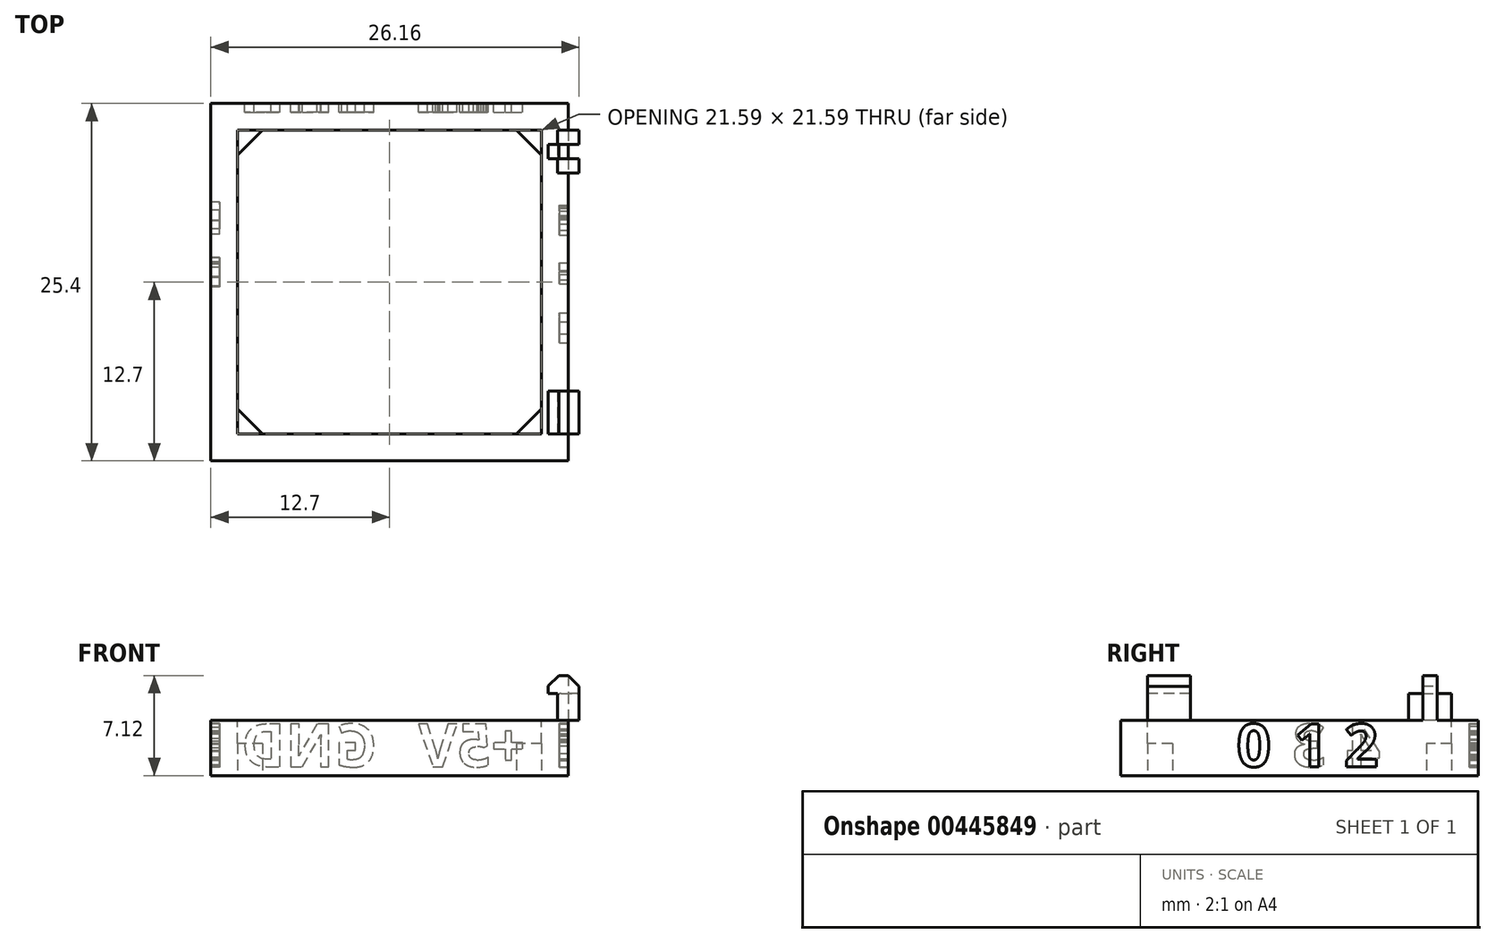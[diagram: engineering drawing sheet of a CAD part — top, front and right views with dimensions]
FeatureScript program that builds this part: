
annotation { "Feature Type Name" : "Feature", "Feature Type Description" : "" }
export const myFeature = defineFeature(function(context is Context, id is Id, definition is map)
    precondition{}
    {
        {
            var Q0;
            Q0=qCreatedBy(makeId("Top.planeOp"),FACE);
            var sketch = newSketch(context, id + "F0", { "sketchPlane" : qUnion([Q0])});
            skLineSegment(sketch, "E0.bottom", {"start": v(10.8, 10.8) * mm, "end": v(-10.8, 10.8) * mm});
            skLineSegment(sketch, "E0.top", {"start": v(10.8, -10.8) * mm, "end": v(-10.8, -10.8) * mm});
            skLineSegment(sketch, "E0.left", {"start": v(10.8, 10.8) * mm, "end": v(10.8, -10.8) * mm});
            skLineSegment(sketch, "E0.right", {"start": v(-10.8, 10.8) * mm, "end": v(-10.8, -10.8) * mm});
            skPoint(sketch, "E0.middle", {"position": v(0, 0) * mm});
            skLineSegment(sketch, "E1.0", {"start": v(12.7, -12.7) * mm, "end": v(-12.7, -12.7) * mm});
            skLineSegment(sketch, "E1.1", {"start": v(12.7, 12.7) * mm, "end": v(12.7, -12.7) * mm});
            skLineSegment(sketch, "E1.2", {"start": v(12.7, 12.7) * mm, "end": v(-12.7, 12.7) * mm});
            skLineSegment(sketch, "E1.3", {"start": v(-12.7, 12.7) * mm, "end": v(-12.7, -12.7) * mm});
            skSolve(sketch);
        }
        {
            var Q0;
            Q0=makeQuery(id+"F0.imprint","IMPRINT",FACE,{"disambiguationData":[TD([[makeQuery(id+"F0.imprint","IMPRINT",EDGE,{"derivedFrom":sQuery(id+"F0.wireOp",EDGE,"E0.bottom")}),1.0]])]});
            var sketch = newSketch(context, id + "F1", { "sketchPlane" : qUnion([Q0])});
            skPoint(sketch, "E2", {"position": v(0, 0) * mm});
            skSolve(sketch);
        }
        {
            var Q0;
            Q0=makeQuery(id+"F0.imprint","IMPRINT",FACE,{"disambiguationData":[TD([[makeQuery(id+"F0.imprint","IMPRINT",EDGE,{"derivedFrom":sQuery(id+"F0.wireOp",EDGE,"E0.bottom")}),-1.0]])]});
            extrude(context, id + "F2", {"entities" : qUnion([Q0]), "oppositeDirection" : true, "depth" : 2.3 * mm});
        }
        {
            var Q0;
            Q0=makeQuery(id+"F0.imprint","IMPRINT",FACE,{"disambiguationData":[TD([[makeQuery(id+"F0.imprint","IMPRINT",EDGE,{"derivedFrom":sQuery(id+"F0.wireOp",EDGE,"E0.bottom")}),-1.0]])]});
            extrude(context, id + "F3", {"entities" : qUnion([Q0]), "operationType" : NewBodyOperationType.ADD, "depth" : 1.65 * mm});
        }
        {
            var Q0;
            {var subQ0=sQuery(id+"F0.wireOp",EDGE,"E1.1");Q0=makeQuery(id+"F33ZesgtKe6OHiI_1.boolean.opBoolean","MERGE",FACE,{"derivedFrom":[makeQuery(id+"Fl4HXPqddT7Ymcp_1.boolean.opBoolean","MERGE",FACE,{"derivedFrom":[makeQuery(id+"F2.opExtrude","SWEPT_FACE",FACE,{"disambiguationData":[OSD([subQ0])]}),makeQuery(id+"Fl4HXPqddT7Ymcp_1.opExtrude","SWEPT_FACE",FACE,{"disambiguationData":[OSD([subQ0])]})]}),makeQuery(id+"F33ZesgtKe6OHiI_1.opExtrude","SWEPT_FACE",FACE,{"disambiguationData":[OSD([sQuery(id+"FHJWVWNGVrHaLrI_1.wireOp",EDGE,"lk0AvFoq-LB85-dOoa-LuWJ-0AeOwgkN9JTX.right")])]})]});}
            var sketch = newSketch(context, id + "F4", { "sketchPlane" : qUnion([Q0])});
            skText(sketch, "E3", { "text": "0", "fontName": "OpenSans-Bold.ttf"});
            skText(sketch, "E4", { "text": "1", "fontName": "OpenSans-Bold.ttf"});
            skText(sketch, "E5", { "text": "2", "fontName": "OpenSans-Bold.ttf"});
            skLineSegment(sketch, "E6.0.0", {"start": v(12.7, -2.29) * mm, "end": v(12.7, 1.65) * mm});
            skLineSegment(sketch, "E6.0.1", {"start": v(12.7, 1.65) * mm, "end": v(-12.7, 1.65) * mm});
            skLineSegment(sketch, "E6.0.2", {"start": v(-12.7, 1.65) * mm, "end": v(-12.7, -2.29) * mm});
            skLineSegment(sketch, "E6.0.3", {"start": v(-12.7, -2.29) * mm, "end": v(12.7, -2.29) * mm});
            skPoint(sketch, "E7.0", {"position": v(0, 0) * mm});
            const initialGuessF4  = {"E3": [-0.00445, -0.00165, 1, 0, 0.00305], "E4": [-0.00038, -0.00165, 1, 0, 0.00305], "E5": [0.00317, -0.00165, 1, 0, 0.00305]};
            skSetInitialGuess(sketch, initialGuessF4);
            skSolve(sketch);
        }
        {
            var Q0;
            Q0=makeQuery(id+"F4.imprint","IMPRINT",FACE,{"disambiguationData":[TD([[makeQuery(id+"F4.imprint","IMPRINT",EDGE,{"derivedFrom":sQuery(id+"F4.wireOp",EDGE,"E3.sketch_text.stroke-0")}),-1.0]])]});
            var Q1;
            Q1=makeQuery(id+"F4.imprint","IMPRINT",FACE,{"disambiguationData":[TD([[makeQuery(id+"F4.imprint","IMPRINT",EDGE,{"derivedFrom":sQuery(id+"F4.wireOp",EDGE,"E4.sketch_text.stroke-0")}),-1.0]])]});
            var Q2;
            Q2=makeQuery(id+"F4.imprint","IMPRINT",FACE,{"disambiguationData":[TD([[makeQuery(id+"F4.imprint","IMPRINT",EDGE,{"derivedFrom":sQuery(id+"F4.wireOp",EDGE,"E5.sketch_text.stroke-0")}),-1.0]])]});
            extrude(context, id + "F5", {"entities" : qUnion([Q0, Q1, Q2]), "operationType" : NewBodyOperationType.REMOVE, "oppositeDirection" : true, "depth" : 0.63 * mm});
        }
        {
            var Q0;
            {var subQ0=sQuery(id+"F0.wireOp",EDGE,"E1.3");Q0=makeQuery(id+"F33ZesgtKe6OHiI_1.boolean.opBoolean","MERGE",FACE,{"derivedFrom":[makeQuery(id+"Fl4HXPqddT7Ymcp_1.boolean.opBoolean","MERGE",FACE,{"derivedFrom":[makeQuery(id+"F2.opExtrude","SWEPT_FACE",FACE,{"disambiguationData":[OSD([subQ0])]}),makeQuery(id+"Fl4HXPqddT7Ymcp_1.opExtrude","SWEPT_FACE",FACE,{"disambiguationData":[OSD([subQ0])]})]}),makeQuery(id+"F33ZesgtKe6OHiI_1.opExtrude","SWEPT_FACE",FACE,{"disambiguationData":[OSD([sQuery(id+"FHJWVWNGVrHaLrI_1.wireOp",EDGE,"lk0AvFoq-LB85-dOoa-LuWJ-0AeOwgkN9JTX.left")])]})]});}
            var sketch = newSketch(context, id + "F6", { "sketchPlane" : qUnion([Q0])});
            skText(sketch, "E8", { "text": "4", "fontName": "OpenSans-Bold.ttf"});
            skText(sketch, "E9", { "text": "3", "fontName": "OpenSans-Bold.ttf"});
            skPoint(sketch, "E10.0", {"position": v(1.9, 1.4) * mm});
            skPoint(sketch, "E11.0", {"position": v(-1.9, 1.4) * mm});
            const initialGuessF6  = {"E8": [-0.00576, -0.00165, 1, 0, 0.00305], "E9": [-0.0019, -0.00165, 1, 0, 0.00305]};
            skSetInitialGuess(sketch, initialGuessF6);
            skSolve(sketch);
        }
        {
            var Q0;
            Q0=makeQuery(id+"F6.imprint","IMPRINT",FACE,{"disambiguationData":[TD([[makeQuery(id+"F6.imprint","IMPRINT",EDGE,{"derivedFrom":sQuery(id+"F6.wireOp",EDGE,"E8.sketch_text.stroke-0")}),-1.0]])]});
            var Q1;
            Q1=makeQuery(id+"F6.imprint","IMPRINT",FACE,{"disambiguationData":[TD([[makeQuery(id+"F6.imprint","IMPRINT",EDGE,{"derivedFrom":sQuery(id+"F6.wireOp",EDGE,"E9.sketch_text.stroke-0")}),-1.0]])]});
            extrude(context, id + "F7", {"entities" : qUnion([Q0, Q1]), "operationType" : NewBodyOperationType.REMOVE, "oppositeDirection" : true, "depth" : 0.63 * mm});
        }
        {
            var Q0;
            {var subQ0=sQuery(id+"F0.wireOp",EDGE,"E1.2");Q0=makeQuery(id+"F3.boolean.opBoolean","MERGE",FACE,{"derivedFrom":[makeQuery(id+"F2.opExtrude","SWEPT_FACE",FACE,{"disambiguationData":[OSD([subQ0])]}),makeQuery(id+"F3.opExtrude","SWEPT_FACE",FACE,{"disambiguationData":[OSD([subQ0])]})]});}
            var sketch = newSketch(context, id + "F8", { "sketchPlane" : qUnion([Q0])});
            skText(sketch, "E12", { "text": "+5V", "fontName": "OpenSans-Bold.ttf"});
            skText(sketch, "E13", { "text": "GND", "fontName": "OpenSans-Bold.ttf"});
            skLineSegment(sketch, "E14.0.0", {"start": v(-10.8, -2.29) * mm, "end": v(-10.8, 1.65) * mm});
            skLineSegment(sketch, "E14.0.2", {"start": v(-10.8, 1.65) * mm, "end": v(-10.8, -2.29) * mm});
            skLineSegment(sketch, "E15.0.0", {"start": v(10.8, -2.29) * mm, "end": v(10.8, 1.65) * mm});
            skLineSegment(sketch, "E15.0.2", {"start": v(10.8, 1.65) * mm, "end": v(10.8, -2.29) * mm});
            const initialGuessF8  = {"E12": [-0.00964, -0.00165, 1, 0, 0.00305], "E13": [0.00088, -0.00165, 1, 0, 0.00305]};
            skSetInitialGuess(sketch, initialGuessF8);
            skSolve(sketch);
        }
        {
            var Q0;
            Q0=qSketchRegion(id+"F8",true);
            extrude(context, id + "F9", {"entities" : qUnion([Q0]), "operationType" : NewBodyOperationType.REMOVE, "oppositeDirection" : true, "depth" : 0.63 * mm});
        }
        {
            var Q0;
            Q0=makeQuery(id+"F2.opExtrude","CAP_FACE",FACE,{"disambiguationData":[OSD([sQuery(id+"F0.wireOp",EDGE,"E0.bottom"),sQuery(id+"F0.wireOp",EDGE,"E0.top"),sQuery(id+"F0.wireOp",EDGE,"E0.left"),sQuery(id+"F0.wireOp",EDGE,"E0.right"),sQuery(id+"F0.wireOp",EDGE,"E1.0"),sQuery(id+"F0.wireOp",EDGE,"E1.1"),sQuery(id+"F0.wireOp",EDGE,"E1.2"),sQuery(id+"F0.wireOp",EDGE,"E1.3")])],"isStart":false});
            var sketch = newSketch(context, id + "F10", { "sketchPlane" : qUnion([Q0])});
            skLineSegment(sketch, "E16", {"start": v(-10.8, 9.02) * mm, "end": v(-9.02, 10.8) * mm});
            skLineSegment(sketch, "E17", {"start": v(-9.02, 10.8) * mm, "end": v(-10.8, 10.8) * mm});
            skLineSegment(sketch, "E18", {"start": v(-10.8, 10.8) * mm, "end": v(-10.8, 9.02) * mm});
            skLineSegment(sketch, "E19", {"start": v(0, 10.8) * mm, "end": v(0, 0) * mm});
            skLineSegment(sketch, "E20", {"start": v(0, 0) * mm, "end": v(10.8, 0) * mm});
            skLineSegment(sketch, "E21.MirrorCS", {"start": v(10.8, 10.8) * mm, "end": v(10.8, 9.02) * mm});
            skLineSegment(sketch, "E22.MirrorCS", {"start": v(9.02, 10.8) * mm, "end": v(10.8, 10.8) * mm});
            skLineSegment(sketch, "E23.MirrorCS", {"start": v(10.8, 9.02) * mm, "end": v(9.02, 10.8) * mm});
            skLineSegment(sketch, "E24.MirrorCS", {"start": v(10.8, -10.8) * mm, "end": v(10.8, -9.02) * mm});
            skLineSegment(sketch, "E25.MirrorCS", {"start": v(10.8, -9.02) * mm, "end": v(9.02, -10.8) * mm});
            skLineSegment(sketch, "E26.MirrorCS", {"start": v(-9.02, -10.8) * mm, "end": v(-10.8, -10.8) * mm});
            skLineSegment(sketch, "E27.MirrorCS", {"start": v(9.02, -10.8) * mm, "end": v(10.8, -10.8) * mm});
            skLineSegment(sketch, "E28.MirrorCS", {"start": v(-10.8, -9.02) * mm, "end": v(-9.02, -10.8) * mm});
            skLineSegment(sketch, "E29.MirrorCS", {"start": v(-10.8, -10.8) * mm, "end": v(-10.8, -9.02) * mm});
            skSolve(sketch);
        }
        {
            var Q0;
            Q0=makeQuery(id+"F10.imprint","IMPRINT",FACE,{"disambiguationData":[TD([[makeQuery(id+"F10.imprint","IMPRINT",EDGE,{"derivedFrom":sQuery(id+"F10.wireOp",EDGE,"E16")}),1.0]])]});
            var Q1;
            Q1=makeQuery(id+"F10.imprint","IMPRINT",FACE,{"disambiguationData":[TD([[makeQuery(id+"F10.imprint","IMPRINT",EDGE,{"derivedFrom":sQuery(id+"F10.wireOp",EDGE,"E26.MirrorCS")}),-1.0]])]});
            var Q2;
            Q2=makeQuery(id+"F10.imprint","IMPRINT",FACE,{"disambiguationData":[TD([[makeQuery(id+"F10.imprint","IMPRINT",EDGE,{"derivedFrom":sQuery(id+"F10.wireOp",EDGE,"E21.MirrorCS")}),1.0]])]});
            var Q3;
            Q3=makeQuery(id+"F10.imprint","IMPRINT",FACE,{"disambiguationData":[TD([[makeQuery(id+"F10.imprint","IMPRINT",EDGE,{"derivedFrom":sQuery(id+"F10.wireOp",EDGE,"E24.MirrorCS")}),1.0]])]});
            var Q4;
            Q4=sQuery(id+"F0.wireOp",VERTEX,"E0.right.end");
            extrude(context, id + "F11", {"entities" : qUnion([Q0, Q1, Q2, Q3]), "operationType" : NewBodyOperationType.ADD, "endBound" : BoundingType.UP_TO_VERTEX, "oppositeDirection" : true, "endBoundEntityVertex" : qUnion([Q4]), "depth" : 25.4 * mm});
        }
        {
            var Q0;
            {var subQ2=sQuery(id+"F0.wireOp",EDGE,"E1.1");var subQ3=sQuery(id+"F0.wireOp",EDGE,"E1.0");Q0=makeQuery(id+"F5.boolean.opBoolean","SPLIT",FACE,{"disambiguationData":[TD([makeQuery(id+"F2.opExtrude","SWEPT_FACE",FACE,{"disambiguationData":[OSD([subQ3])]})])],"derivedFrom":makeQuery(id+"F3.boolean.opBoolean","MERGE",FACE,{"derivedFrom":[makeQuery(id+"F2.opExtrude","SWEPT_FACE",FACE,{"disambiguationData":[OSD([subQ2])]}),makeQuery(id+"F3.opExtrude","SWEPT_FACE",FACE,{"disambiguationData":[OSD([subQ2])]})]})});}
            var sketch = newSketch(context, id + "F12", { "sketchPlane" : qUnion([Q0])});
            skLineSegment(sketch, "E30.bottom", {"start": v(7.75, -1.52) * mm, "end": v(10.8, -1.52) * mm});
            skLineSegment(sketch, "E30.top", {"start": v(7.75, 4.83) * mm, "end": v(10.8, 4.83) * mm});
            skLineSegment(sketch, "E30.left", {"start": v(7.75, -1.52) * mm, "end": v(7.75, 4.83) * mm});
            skLineSegment(sketch, "E30.right", {"start": v(10.8, -1.52) * mm, "end": v(10.8, 4.83) * mm});
            skLineSegment(sketch, "E31.bottom", {"start": v(7.75, 4.83) * mm, "end": v(8.76, 4.83) * mm});
            skLineSegment(sketch, "E31.top", {"start": v(7.75, -1.52) * mm, "end": v(8.76, -1.52) * mm});
            skLineSegment(sketch, "E31.left", {"start": v(7.75, 4.83) * mm, "end": v(7.75, -1.52) * mm});
            skLineSegment(sketch, "E31.right", {"start": v(8.76, 4.83) * mm, "end": v(8.76, -1.52) * mm});
            skLineSegment(sketch, "E32.bottom", {"start": v(10.8, 4.83) * mm, "end": v(9.78, 4.83) * mm});
            skLineSegment(sketch, "E32.top", {"start": v(10.8, -1.52) * mm, "end": v(9.78, -1.52) * mm});
            skLineSegment(sketch, "E32.left", {"start": v(10.8, 4.83) * mm, "end": v(10.8, -1.52) * mm});
            skLineSegment(sketch, "E32.right", {"start": v(9.78, 4.83) * mm, "end": v(9.78, -1.52) * mm});
            skLineSegment(sketch, "E33.top", {"start": v(7.75, 3.56) * mm, "end": v(10.8, 3.56) * mm});
            skLineSegment(sketch, "E33.left", {"start": v(7.75, 4.83) * mm, "end": v(7.75, 3.56) * mm});
            skLineSegment(sketch, "E33.right", {"start": v(10.8, 4.83) * mm, "end": v(10.8, 3.56) * mm});
            skLineSegment(sketch, "E34", {"start": v(0, 1.65) * mm, "end": v(0, -2.29) * mm});
            skLineSegment(sketch, "E35.MirrorCS", {"start": v(-7.75, 4.83) * mm, "end": v(-7.75, 3.56) * mm});
            skLineSegment(sketch, "E36.MirrorCS", {"start": v(-10.8, 4.83) * mm, "end": v(-10.8, 3.56) * mm});
            skLineSegment(sketch, "E37.MirrorCS", {"start": v(-10.8, 4.83) * mm, "end": v(-9.78, 4.83) * mm});
            skLineSegment(sketch, "E38.MirrorCS", {"start": v(-7.75, 4.83) * mm, "end": v(-10.8, 4.83) * mm});
            skLineSegment(sketch, "E39.MirrorCS", {"start": v(-7.75, -1.52) * mm, "end": v(-7.75, 4.83) * mm});
            skLineSegment(sketch, "E40.MirrorCS", {"start": v(-10.8, -1.52) * mm, "end": v(-10.8, 4.83) * mm});
            skLineSegment(sketch, "E41.MirrorCS", {"start": v(-7.75, 4.83) * mm, "end": v(-8.76, 4.83) * mm});
            skLineSegment(sketch, "E42.MirrorCS", {"start": v(-7.75, 3.56) * mm, "end": v(-10.8, 3.56) * mm});
            skLineSegment(sketch, "E43.MirrorCS", {"start": v(-7.75, -1.52) * mm, "end": v(-10.8, -1.52) * mm});
            skLineSegment(sketch, "E44.MirrorCS", {"start": v(-7.75, -1.52) * mm, "end": v(-8.76, -1.52) * mm});
            skLineSegment(sketch, "E45.MirrorCS", {"start": v(-7.75, 4.83) * mm, "end": v(-7.75, -1.52) * mm});
            skLineSegment(sketch, "E46.MirrorCS", {"start": v(-8.76, 4.83) * mm, "end": v(-8.76, -1.52) * mm});
            skLineSegment(sketch, "E47.MirrorCS", {"start": v(-10.8, -1.52) * mm, "end": v(-9.78, -1.52) * mm});
            skLineSegment(sketch, "E48.MirrorCS", {"start": v(-10.8, 4.83) * mm, "end": v(-10.8, -1.52) * mm});
            skLineSegment(sketch, "E49.MirrorCS", {"start": v(-9.78, 4.83) * mm, "end": v(-9.78, -1.52) * mm});
            skSolve(sketch);
        }
        {
            var Q0;
            {var subQ0=sQuery(id+"F12.wireOp",EDGE,"E33.top");var subQ1=sQuery(id+"F12.wireOp",EDGE,"E31.right");var subQ2=makeQuery(id+"F12.imprint","INTERSECT",VERTEX,{"derivedFrom":[subQ1,subQ0]});Q0=makeQuery(id+"F12.imprint","IMPRINT",FACE,{"disambiguationData":[TD([[makeQuery(id+"F12.imprint","IMPRINT",EDGE,{"disambiguationData":[TD([[subQ2,-1.0]])],"derivedFrom":subQ1}),1.0]])]});}
            var Q1;
            {var subQ0=sQuery(id+"F12.wireOp",EDGE,"E33.top");var subQ5=sQuery(id+"F12.wireOp",EDGE,"E32.right");var subQ6=makeQuery(id+"F12.imprint","INTERSECT",VERTEX,{"derivedFrom":[subQ5,subQ0]});Q1=makeQuery(id+"F12.imprint","IMPRINT",FACE,{"disambiguationData":[TD([[makeQuery(id+"F12.imprint","IMPRINT",EDGE,{"disambiguationData":[TD([[subQ6,-1.0]])],"derivedFrom":subQ5}),1.0]])]});}
            var Q2;
            {var subQ0=sQuery(id+"F12.wireOp",EDGE,"E33.top");var subQ5=sQuery(id+"F12.wireOp",EDGE,"E31.right");var subQ6=makeQuery(id+"F12.imprint","INTERSECT",VERTEX,{"derivedFrom":[subQ5,subQ0]});Q2=makeQuery(id+"F12.imprint","IMPRINT",FACE,{"disambiguationData":[TD([[makeQuery(id+"F12.imprint","IMPRINT",EDGE,{"disambiguationData":[TD([[subQ6,-1.0]])],"derivedFrom":subQ5}),-1.0]])]});}
            var Q3;
            {var subQ0=sQuery(id+"F12.wireOp",EDGE,"E45.MirrorCS");var subQ1=sQuery(id+"F12.wireOp",EDGE,"E42.MirrorCS");var subQ2=makeQuery(id+"F12.imprint","INTERSECT",VERTEX,{"derivedFrom":[subQ1,subQ0]});Q3=makeQuery(id+"F12.imprint","IMPRINT",FACE,{"disambiguationData":[TD([[makeQuery(id+"F12.imprint","IMPRINT",EDGE,{"disambiguationData":[TD([[subQ2,-1.0]])],"derivedFrom":subQ1}),1.0]])]});}
            var Q4;
            {var subQ0=sQuery(id+"F12.wireOp",EDGE,"E46.MirrorCS");var subQ1=sQuery(id+"F12.wireOp",EDGE,"E42.MirrorCS");var subQ2=makeQuery(id+"F12.imprint","INTERSECT",VERTEX,{"derivedFrom":[subQ1,subQ0]});Q4=makeQuery(id+"F12.imprint","IMPRINT",FACE,{"disambiguationData":[TD([[makeQuery(id+"F12.imprint","IMPRINT",EDGE,{"disambiguationData":[TD([[subQ2,-1.0]])],"derivedFrom":subQ1}),1.0]])]});}
            var Q5;
            {var subQ0=sQuery(id+"F12.wireOp",EDGE,"E48.MirrorCS");var subQ1=sQuery(id+"F12.wireOp",EDGE,"E42.MirrorCS");var subQ2=makeQuery(id+"F12.imprint","INTERSECT",VERTEX,{"derivedFrom":[subQ1,subQ0]});Q5=makeQuery(id+"F12.imprint","IMPRINT",FACE,{"disambiguationData":[TD([[makeQuery(id+"F12.imprint","IMPRINT",EDGE,{"disambiguationData":[TD([[subQ2,1.0]])],"derivedFrom":subQ1}),1.0]])]});}
            extrude(context, id + "F13", {"entities" : qUnion([Q0, Q1, Q2, Q3, Q4, Q5]), "operationType" : NewBodyOperationType.ADD, "oppositeDirection" : true, "depth" : 0.76 * mm});
        }
        {
            var Q0;
            {var subQ0=sQuery(id+"F12.wireOp",EDGE,"E44.MirrorCS");Q0=makeQuery(id+"F12.imprint","IMPRINT",FACE,{"disambiguationData":[TD([[makeQuery(id+"F12.imprint","IMPRINT",EDGE,{"derivedFrom":subQ0}),-1.0]])]});}
            var Q1;
            {var subQ0=sQuery(id+"F12.wireOp",EDGE,"E47.MirrorCS");Q1=makeQuery(id+"F12.imprint","IMPRINT",FACE,{"disambiguationData":[TD([[makeQuery(id+"F12.imprint","IMPRINT",EDGE,{"derivedFrom":subQ0}),1.0]])]});}
            var Q2;
            {var subQ0=sQuery(id+"F12.wireOp",EDGE,"E48.MirrorCS");var subQ1=sQuery(id+"F12.wireOp",EDGE,"E42.MirrorCS");var subQ2=makeQuery(id+"F12.imprint","INTERSECT",VERTEX,{"derivedFrom":[subQ1,subQ0]});Q2=makeQuery(id+"F12.imprint","IMPRINT",FACE,{"disambiguationData":[TD([[makeQuery(id+"F12.imprint","IMPRINT",EDGE,{"disambiguationData":[TD([[subQ2,1.0]])],"derivedFrom":subQ1}),1.0]])]});}
            var Q3;
            {var subQ0=sQuery(id+"F12.wireOp",EDGE,"E48.MirrorCS");var subQ1=sQuery(id+"F12.wireOp",EDGE,"E42.MirrorCS");var subQ2=makeQuery(id+"F12.imprint","INTERSECT",VERTEX,{"derivedFrom":[subQ1,subQ0]});Q3=makeQuery(id+"F12.imprint","IMPRINT",FACE,{"disambiguationData":[TD([[makeQuery(id+"F12.imprint","IMPRINT",EDGE,{"disambiguationData":[TD([[subQ2,1.0]])],"derivedFrom":subQ1}),-1.0]])]});}
            var Q4;
            {var subQ0=sQuery(id+"F12.wireOp",EDGE,"E45.MirrorCS");var subQ1=sQuery(id+"F12.wireOp",EDGE,"E42.MirrorCS");var subQ2=makeQuery(id+"F12.imprint","INTERSECT",VERTEX,{"derivedFrom":[subQ1,subQ0]});Q4=makeQuery(id+"F12.imprint","IMPRINT",FACE,{"disambiguationData":[TD([[makeQuery(id+"F12.imprint","IMPRINT",EDGE,{"disambiguationData":[TD([[subQ2,-1.0]])],"derivedFrom":subQ1}),-1.0]])]});}
            var Q5;
            {var subQ0=sQuery(id+"F12.wireOp",EDGE,"E45.MirrorCS");var subQ1=sQuery(id+"F12.wireOp",EDGE,"E42.MirrorCS");var subQ2=makeQuery(id+"F12.imprint","INTERSECT",VERTEX,{"derivedFrom":[subQ1,subQ0]});Q5=makeQuery(id+"F12.imprint","IMPRINT",FACE,{"disambiguationData":[TD([[makeQuery(id+"F12.imprint","IMPRINT",EDGE,{"disambiguationData":[TD([[subQ2,-1.0]])],"derivedFrom":subQ1}),1.0]])]});}
            var Q6;
            {var subQ5=sQuery(id+"F12.wireOp",EDGE,"E33.left");Q6=makeQuery(id+"F12.imprint","IMPRINT",FACE,{"disambiguationData":[TD([[makeQuery(id+"F12.imprint","IMPRINT",EDGE,{"derivedFrom":subQ5}),1.0]])]});}
            var Q7;
            {var subQ0=sQuery(id+"F12.wireOp",EDGE,"E33.top");var subQ5=sQuery(id+"F12.wireOp",EDGE,"E32.right");var subQ6=makeQuery(id+"F12.imprint","INTERSECT",VERTEX,{"derivedFrom":[subQ5,subQ0]});Q7=makeQuery(id+"F12.imprint","IMPRINT",FACE,{"disambiguationData":[TD([[makeQuery(id+"F12.imprint","IMPRINT",EDGE,{"disambiguationData":[TD([[subQ6,-1.0]])],"derivedFrom":subQ5}),1.0]])]});}
            var Q8;
            {var subQ0=sQuery(id+"F12.wireOp",EDGE,"E33.top");var subQ5=sQuery(id+"F12.wireOp",EDGE,"E31.right");var subQ6=makeQuery(id+"F12.imprint","INTERSECT",VERTEX,{"derivedFrom":[subQ5,subQ0]});Q8=makeQuery(id+"F12.imprint","IMPRINT",FACE,{"disambiguationData":[TD([[makeQuery(id+"F12.imprint","IMPRINT",EDGE,{"disambiguationData":[TD([[subQ6,-1.0]])],"derivedFrom":subQ5}),-1.0]])]});}
            var Q9;
            {var subQ5=sQuery(id+"F12.wireOp",EDGE,"E33.right");Q9=makeQuery(id+"F12.imprint","IMPRINT",FACE,{"disambiguationData":[TD([[makeQuery(id+"F12.imprint","IMPRINT",EDGE,{"derivedFrom":subQ5}),-1.0]])]});}
            var Q10;
            {var subQ0=sQuery(id+"F12.wireOp",EDGE,"E31.top");Q10=makeQuery(id+"F12.imprint","IMPRINT",FACE,{"disambiguationData":[TD([[makeQuery(id+"F12.imprint","IMPRINT",EDGE,{"derivedFrom":subQ0}),1.0]])]});}
            var Q11;
            {var subQ0=sQuery(id+"F12.wireOp",EDGE,"E32.top");Q11=makeQuery(id+"F12.imprint","IMPRINT",FACE,{"disambiguationData":[TD([[makeQuery(id+"F12.imprint","IMPRINT",EDGE,{"derivedFrom":subQ0}),-1.0]])]});}
            extrude(context, id + "F14", {"entities" : qUnion([Q0, Q1, Q2, Q3, Q4, Q5, Q6, Q7, Q8, Q9, Q10, Q11]), "operationType" : NewBodyOperationType.ADD, "depth" : 0.76 * mm});
        }
        {
            var Q0;
            {var subQ5=sQuery(id+"F12.wireOp",EDGE,"E33.left");Q0=makeQuery(id+"F12.imprint","IMPRINT",FACE,{"disambiguationData":[TD([[makeQuery(id+"F12.imprint","IMPRINT",EDGE,{"derivedFrom":subQ5}),1.0]])]});}
            var Q1;
            {var subQ0=sQuery(id+"F12.wireOp",EDGE,"E30.top");var subQ1=sQuery(id+"F12.wireOp",EDGE,"E31.right");var subQ2=makeQuery(id+"F12.imprint","INTERSECT",VERTEX,{"derivedFrom":[subQ1,subQ0]});Q1=makeQuery(id+"F12.imprint","IMPRINT",FACE,{"disambiguationData":[TD([[makeQuery(id+"F12.imprint","IMPRINT",EDGE,{"disambiguationData":[TD([[subQ2,-1.0]])],"derivedFrom":subQ1}),1.0]])]});}
            var Q2;
            {var subQ5=sQuery(id+"F12.wireOp",EDGE,"E33.right");Q2=makeQuery(id+"F12.imprint","IMPRINT",FACE,{"disambiguationData":[TD([[makeQuery(id+"F12.imprint","IMPRINT",EDGE,{"derivedFrom":subQ5}),-1.0]])]});}
            var Q3;
            {var subQ0=sQuery(id+"F12.wireOp",EDGE,"E48.MirrorCS");var subQ1=sQuery(id+"F12.wireOp",EDGE,"E42.MirrorCS");var subQ2=makeQuery(id+"F12.imprint","INTERSECT",VERTEX,{"derivedFrom":[subQ1,subQ0]});Q3=makeQuery(id+"F12.imprint","IMPRINT",FACE,{"disambiguationData":[TD([[makeQuery(id+"F12.imprint","IMPRINT",EDGE,{"disambiguationData":[TD([[subQ2,1.0]])],"derivedFrom":subQ1}),-1.0]])]});}
            var Q4;
            {var subQ0=sQuery(id+"F12.wireOp",EDGE,"E46.MirrorCS");var subQ1=sQuery(id+"F12.wireOp",EDGE,"E42.MirrorCS");var subQ2=makeQuery(id+"F12.imprint","INTERSECT",VERTEX,{"derivedFrom":[subQ1,subQ0]});Q4=makeQuery(id+"F12.imprint","IMPRINT",FACE,{"disambiguationData":[TD([[makeQuery(id+"F12.imprint","IMPRINT",EDGE,{"disambiguationData":[TD([[subQ2,-1.0]])],"derivedFrom":subQ1}),-1.0]])]});}
            var Q5;
            {var subQ0=sQuery(id+"F12.wireOp",EDGE,"E45.MirrorCS");var subQ1=sQuery(id+"F12.wireOp",EDGE,"E42.MirrorCS");var subQ2=makeQuery(id+"F12.imprint","INTERSECT",VERTEX,{"derivedFrom":[subQ1,subQ0]});Q5=makeQuery(id+"F12.imprint","IMPRINT",FACE,{"disambiguationData":[TD([[makeQuery(id+"F12.imprint","IMPRINT",EDGE,{"disambiguationData":[TD([[subQ2,-1.0]])],"derivedFrom":subQ1}),-1.0]])]});}
            extrude(context, id + "F15", {"entities" : qUnion([Q0, Q1, Q2, Q3, Q4, Q5]), "operationType" : NewBodyOperationType.ADD, "oppositeDirection" : true, "depth" : 0.07 * 19.05 * mm});
        }
        {
            var Q0;
            {var subQ0=sQuery(id+"F12.wireOp",EDGE,"E30.top");Q0=makeQuery(id+"F14.opExtrude","CAP_EDGE",EDGE,{"disambiguationData":[OSD([subQ0]),TDD([makeQuery(id+"F12.imprint","IMPRINT",EDGE,{"disambiguationData":[TD([[makeQuery(id+"F12.imprint","INTERSECT",VERTEX,{"derivedFrom":[sQuery(id+"F12.wireOp",EDGE,"E32.right"),subQ0]}),-1.0]])],"derivedFrom":subQ0})])],"isStart":false});}
            var Q1;
            {var subQ0=sQuery(id+"F12.wireOp",EDGE,"E30.top");Q1=makeQuery(id+"F14.opExtrude","CAP_EDGE",EDGE,{"disambiguationData":[OSD([subQ0]),TDD([makeQuery(id+"F12.imprint","IMPRINT",EDGE,{"disambiguationData":[TD([[makeQuery(id+"F12.imprint","INTERSECT",VERTEX,{"derivedFrom":[sQuery(id+"F12.wireOp",EDGE,"E31.right"),subQ0]}),1.0]])],"derivedFrom":subQ0})])],"isStart":false});}
            var Q2;
            Q2=makeQuery(id+"F14.opExtrude","CAP_EDGE",EDGE,{"disambiguationData":[OSD([sQuery(id+"F12.wireOp",EDGE,"E31.top")])],"isStart":false});
            var Q3;
            Q3=makeQuery(id+"F14.opExtrude","CAP_EDGE",EDGE,{"disambiguationData":[OSD([sQuery(id+"F12.wireOp",EDGE,"E32.top")])],"isStart":false});
            var Q4;
            {var subQ0=sQuery(id+"F12.wireOp",EDGE,"E38.MirrorCS");Q4=makeQuery(id+"F14.opExtrude","CAP_EDGE",EDGE,{"disambiguationData":[OSD([subQ0]),TDD([makeQuery(id+"F12.imprint","IMPRINT",EDGE,{"disambiguationData":[TD([[makeQuery(id+"F12.imprint","INTERSECT",VERTEX,{"derivedFrom":[sQuery(id+"F12.wireOp",EDGE,"E45.MirrorCS"),subQ0]}),-1.0]])],"derivedFrom":subQ0})])],"isStart":false});}
            var Q5;
            {var subQ0=sQuery(id+"F12.wireOp",EDGE,"E38.MirrorCS");Q5=makeQuery(id+"F14.opExtrude","CAP_EDGE",EDGE,{"disambiguationData":[OSD([subQ0]),TDD([makeQuery(id+"F12.imprint","IMPRINT",EDGE,{"disambiguationData":[TD([[makeQuery(id+"F12.imprint","INTERSECT",VERTEX,{"derivedFrom":[sQuery(id+"F12.wireOp",EDGE,"E48.MirrorCS"),subQ0]}),1.0]])],"derivedFrom":subQ0})])],"isStart":false});}
            var Q6;
            Q6=makeQuery(id+"F14.opExtrude","CAP_EDGE",EDGE,{"disambiguationData":[OSD([sQuery(id+"F12.wireOp",EDGE,"E47.MirrorCS")])],"isStart":false});
            var Q7;
            Q7=makeQuery(id+"F14.opExtrude","CAP_EDGE",EDGE,{"disambiguationData":[OSD([sQuery(id+"F12.wireOp",EDGE,"E44.MirrorCS")])],"isStart":false});
            chamfer(context, id + "F16", {"entities" : qUnion([Q0, Q1, Q2, Q3, Q4, Q5, Q6, Q7]), "width" : 0.76 * mm, "tangentPropagation" : true});
        }
        {
            var Q0;
            Q0=makeQuery(id+"F15.opExtrude","CAP_EDGE",EDGE,{"disambiguationData":[OSD([sQuery(id+"F12.wireOp",EDGE,"E30.top")])],"isStart":false});
            var Q1;
            Q1=makeQuery(id+"F15.opExtrude","CAP_EDGE",EDGE,{"disambiguationData":[OSD([sQuery(id+"F12.wireOp",EDGE,"E38.MirrorCS")])],"isStart":false});
            chamfer(context, id + "F17", {"entities" : qUnion([Q0, Q1]), "width" : 0.75 * mm, "tangentPropagation" : true});
        }
        {
            var Q0;
            Q0=makeQuery(id+"F13.opExtrude","CAP_EDGE",EDGE,{"disambiguationData":[OSD([sQuery(id+"F12.wireOp",EDGE,"E33.top")])],"isStart":false});
            var Q1;
            Q1=makeQuery(id+"F13.opExtrude","CAP_EDGE",EDGE,{"disambiguationData":[OSD([sQuery(id+"F12.wireOp",EDGE,"E42.MirrorCS")])],"isStart":false});
            fillet(context, id + "F18", {"entities" : qUnion([Q0, Q1]), "radius" : 0.25 * mm, "tangentPropagation" : true, "allowEdgeOverflow" : false});
        }
    });
